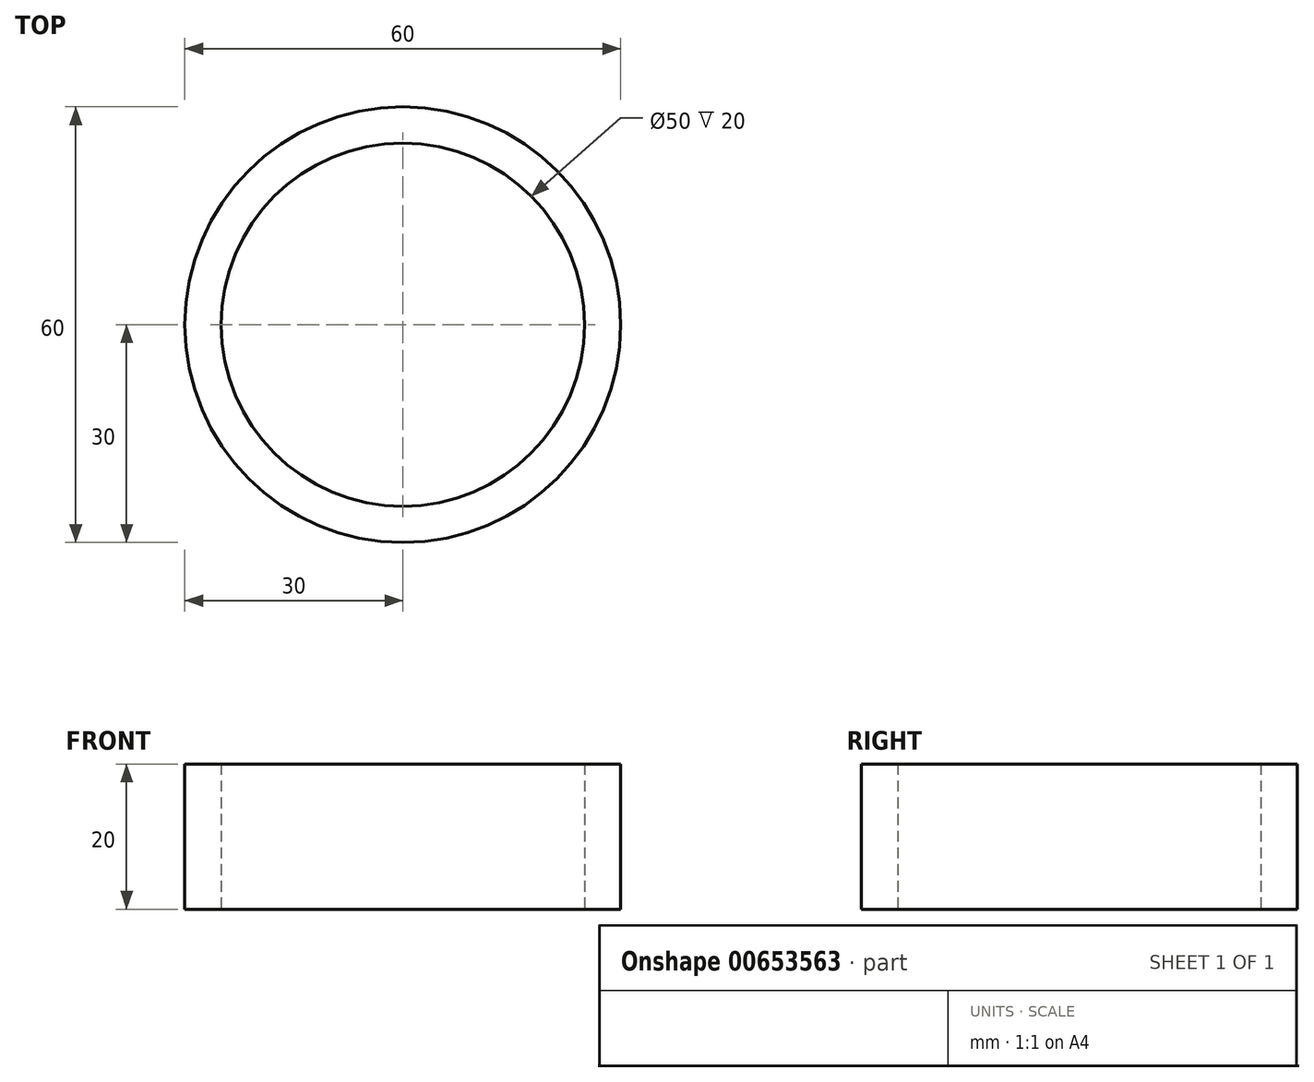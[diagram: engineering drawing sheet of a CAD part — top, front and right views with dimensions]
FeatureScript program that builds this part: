
annotation { "Feature Type Name" : "Feature", "Feature Type Description" : "" }
export const myFeature = defineFeature(function(context is Context, id is Id, definition is map)
    precondition{}
    {
        {
            var Q0;
            Q0=qCreatedBy(makeId("Top.planeOp"),FACE);
            var sketch = newSketch(context, id + "F0", { "sketchPlane" : qUnion([Q0])});
            skCircle(sketch, "E0", {"center": v(0, 0) * mm, "radius": 30 * mm});
            skCircle(sketch, "E1", {"center": v(0, 0) * mm, "radius": 25 * mm});
            skSolve(sketch);
        }
        {
            var Q0;
            Q0=makeQuery(id+"F0.imprint","IMPRINT",FACE,{"disambiguationData":[TD([[makeQuery(id+"F0.imprint","IMPRINT",EDGE,{"derivedFrom":sQuery(id+"F0.wireOp",EDGE,"E0")}),1.0]])]});
            extrude(context, id + "F1", {"entities" : qUnion([Q0]), "depth" : 20 * mm, "offsetDistance" : 25 * mm});
        }
    });
